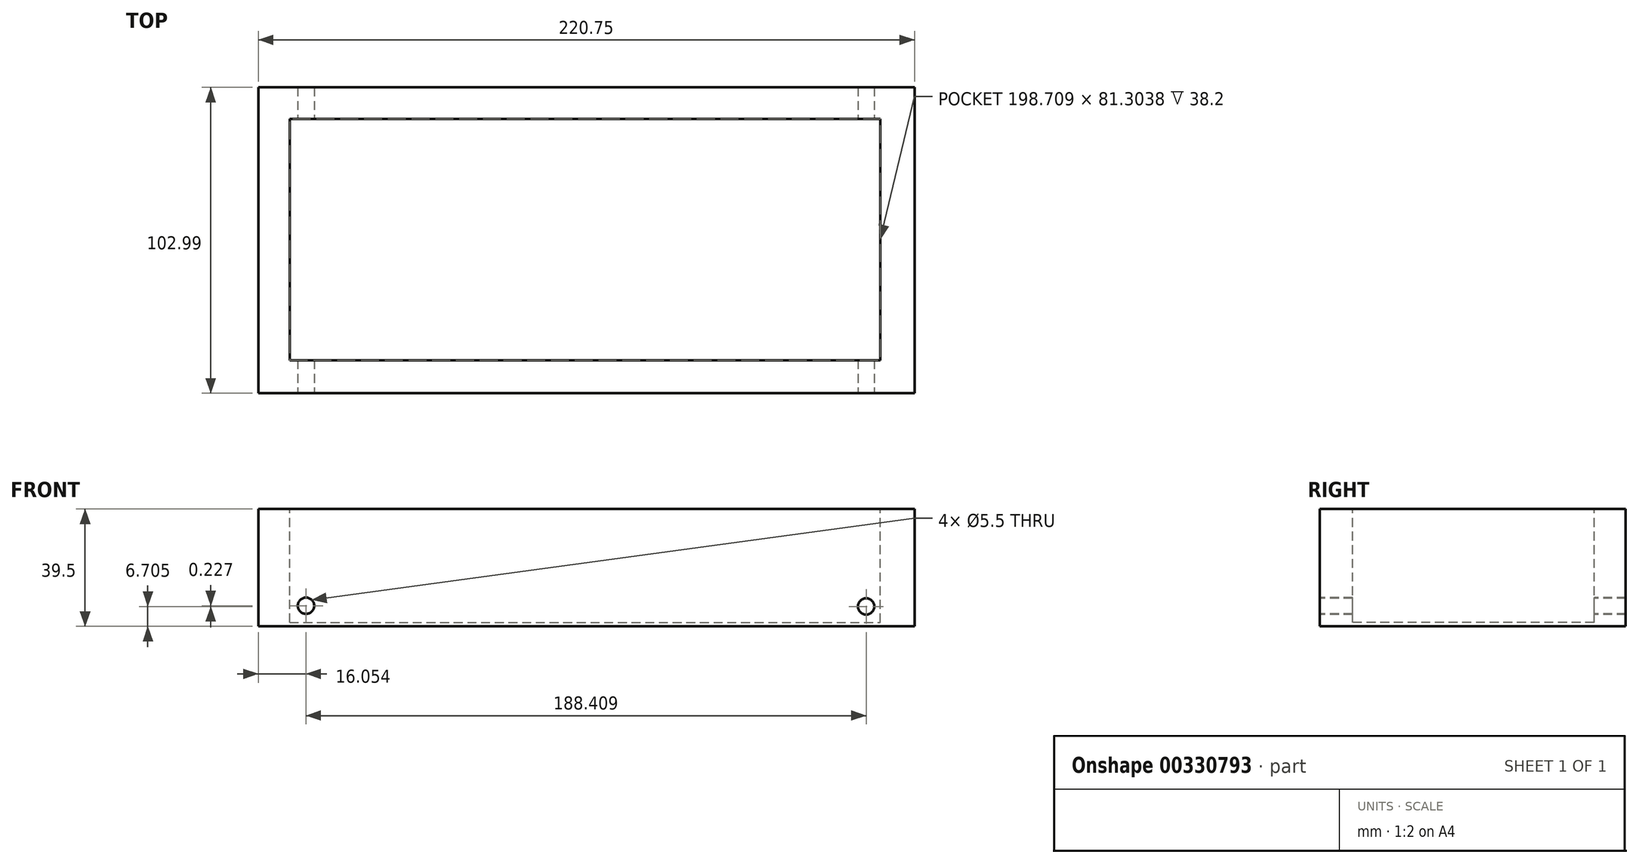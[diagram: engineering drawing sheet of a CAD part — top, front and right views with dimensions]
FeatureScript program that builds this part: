
annotation { "Feature Type Name" : "Feature", "Feature Type Description" : "" }
export const myFeature = defineFeature(function(context is Context, id is Id, definition is map)
    precondition{}
    {
        {
            var Q0;
            Q0=qCreatedBy(makeId("Top.planeOp"),FACE);
            var sketch = newSketch(context, id + "F0", { "sketchPlane" : qUnion([Q0])});
            skLineSegment(sketch, "E0.bottom", {"start": v(-99.52, 43.76) * mm, "end": v(121.23, 43.76) * mm});
            skLineSegment(sketch, "E0.top", {"start": v(-99.52, -59.23) * mm, "end": v(121.23, -59.23) * mm});
            skLineSegment(sketch, "E0.left", {"start": v(-99.52, 43.76) * mm, "end": v(-99.52, -59.23) * mm});
            skLineSegment(sketch, "E0.right", {"start": v(121.23, 43.76) * mm, "end": v(121.23, -59.23) * mm});
            skSolve(sketch);
        }
        {
            var Q0;
            Q0=makeQuery(id+"F0.imprint","IMPRINT",FACE,{"disambiguationData":[TD([[makeQuery(id+"F0.imprint","IMPRINT",EDGE,{"derivedFrom":sQuery(id+"F0.wireOp",EDGE,"E0.bottom")}),-1.0]])]});
            extrude(context, id + "F1", {"entities" : qUnion([Q0]), "depth" : 39.5 * mm});
        }
        {
            var Q0;
            Q0=makeQuery(id+"F1.opExtrude","CAP_FACE",FACE,{"disambiguationData":[OSD([sQuery(id+"F0.wireOp",EDGE,"E0.bottom"),sQuery(id+"F0.wireOp",EDGE,"E0.top"),sQuery(id+"F0.wireOp",EDGE,"E0.left"),sQuery(id+"F0.wireOp",EDGE,"E0.right")])],"isStart":false});
            var sketch = newSketch(context, id + "F2", { "sketchPlane" : qUnion([Q0])});
            skLineSegment(sketch, "E1.bottom", {"start": v(-88.95, 33.17) * mm, "end": v(109.76, 33.17) * mm});
            skLineSegment(sketch, "E1.top", {"start": v(-88.95, -48.13) * mm, "end": v(109.76, -48.13) * mm});
            skLineSegment(sketch, "E1.left", {"start": v(-88.95, 33.17) * mm, "end": v(-88.95, -48.13) * mm});
            skLineSegment(sketch, "E1.right", {"start": v(109.76, 33.17) * mm, "end": v(109.76, -48.13) * mm});
            skSolve(sketch);
        }
        {
            var Q0;
            Q0=makeQuery(id+"F2.imprint","IMPRINT",FACE,{"disambiguationData":[TD([[makeQuery(id+"F2.imprint","IMPRINT",EDGE,{"derivedFrom":sQuery(id+"F2.wireOp",EDGE,"E1.bottom")}),-1.0]])]});
            extrude(context, id + "F3", {"entities" : qUnion([Q0]), "operationType" : NewBodyOperationType.REMOVE, "oppositeDirection" : true, "depth" : 38.2 * mm});
        }
        {
            var Q0;
            Q0=makeQuery(id+"F1.opExtrude","SWEPT_FACE",FACE,{"disambiguationData":[OSD([sQuery(id+"F0.wireOp",EDGE,"E0.top")])]});
            var sketch = newSketch(context, id + "F4", { "sketchPlane" : qUnion([Q0])});
            skPoint(sketch, "E2", {"position": v(-83.47, 6.93) * mm});
            skPoint(sketch, "E3", {"position": v(104.94, 6.7) * mm});
            skSolve(sketch);
        }
        {
            var Q0;
            Q0=sQuery(id+"F4.wireOp",VERTEX,"E2");
            var Q1;
            Q1=sQuery(id+"F4.wireOp",VERTEX,"E3");
            var Q2;
            Q2=makeQuery(id+"F1.opExtrude","SWEPT_BODY",BODY,{"disambiguationData":[OSD([sQuery(id+"F0.wireOp",EDGE,"E0.bottom"),sQuery(id+"F0.wireOp",EDGE,"E0.top"),sQuery(id+"F0.wireOp",EDGE,"E0.left"),sQuery(id+"F0.wireOp",EDGE,"E0.right")])]});
            hole(context, id + "F5", {"style" : HoleStyle.SIMPLE, "endStyle" : HoleEndStyle.THROUGH, "holeDiameter" : 5.5 * mm, "tappedDepth" : 12 * mm, "tapClearance" : 3, "locations" : qUnion([Q0, Q1]), "scope" : qUnion([Q2])});
        }
    });
